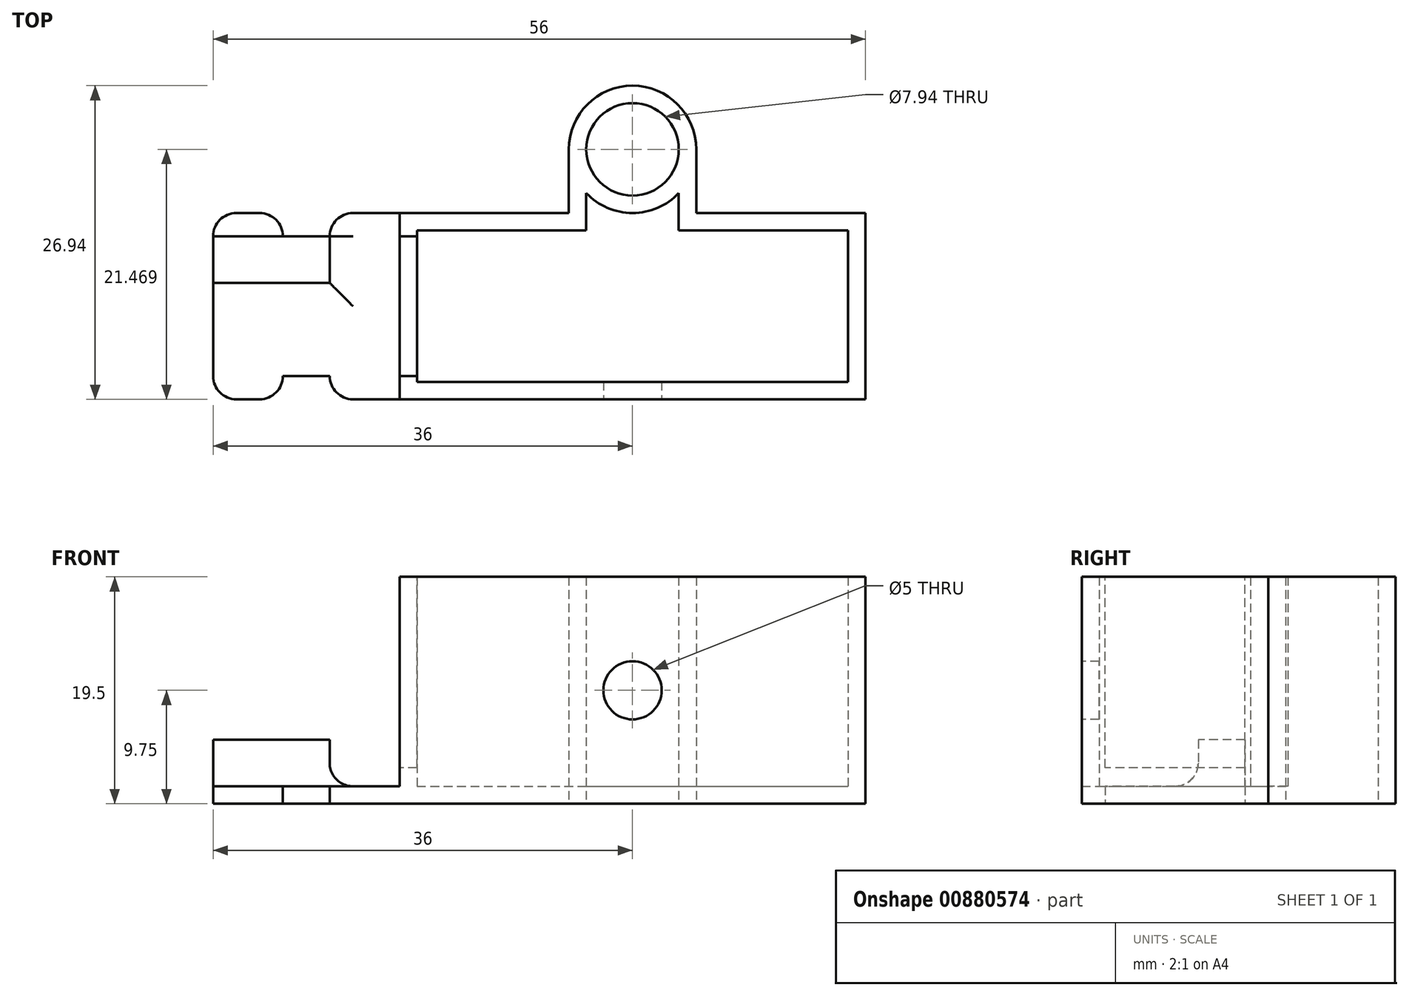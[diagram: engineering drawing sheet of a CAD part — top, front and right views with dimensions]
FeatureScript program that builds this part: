
annotation { "Feature Type Name" : "Feature", "Feature Type Description" : "" }
export const myFeature = defineFeature(function(context is Context, id is Id, definition is map)
    precondition{}
    {
        {
            var Q0;
            Q0=qCreatedBy(makeId("Top.planeOp"),FACE);
            var sketch = newSketch(context, id + "F0", { "sketchPlane" : qUnion([Q0])});
            skLineSegment(sketch, "E0.bottom", {"start": v(0, 0) * mm, "end": v(37, 0) * mm, "construction": true});
            skLineSegment(sketch, "E0.top", {"start": v(0, 13) * mm, "end": v(37, 13) * mm, "construction": true});
            skLineSegment(sketch, "E0.left", {"start": v(0, 0) * mm, "end": v(0, 13) * mm, "construction": true});
            skLineSegment(sketch, "E0.right", {"start": v(37, 0) * mm, "end": v(37, 13) * mm, "construction": true});
            skLineSegment(sketch, "E1.0", {"start": v(-1.5, -1.5) * mm, "end": v(-1.5, 14.5) * mm});
            skLineSegment(sketch, "E1.1", {"start": v(-1.5, -1.5) * mm, "end": v(38.5, -1.5) * mm});
            skLineSegment(sketch, "E1.2", {"start": v(38.5, -1.5) * mm, "end": v(38.5, 14.5) * mm});
            skLineSegment(sketch, "E1.3", {"start": v(-1.5, 14.5) * mm, "end": v(13.03, 14.5) * mm});
            skLineSegment(sketch, "E2", {"start": v(18.5, 14.5) * mm, "end": v(18.5, 25.44) * mm, "construction": true});
            skCircle(sketch, "E3", {"center": v(18.5, 19.97) * mm, "radius": 3.97 * mm});
            skArc(sketch, "E4.0", {"start": v(23.97, 19.97) * mm, "mid": v(18.5, 25.44) * mm, "end": v(13.03, 19.97) * mm});
            skLineSegment(sketch, "E5", {"start": v(23.97, 14.5) * mm, "end": v(23.97, 19.97) * mm});
            skLineSegment(sketch, "E6", {"start": v(13.03, 14.5) * mm, "end": v(13.03, 19.97) * mm});
            skLineSegment(sketch, "E7.trimOffspring", {"start": v(23.97, 14.5) * mm, "end": v(38.5, 14.5) * mm});
            skSolve(sketch);
        }
        {
            var Q0;
            Q0 = qSketchRegion(id + "F0", true);
            extrude(context, id + "F1", {"entities" : qUnion([Q0]), "depth" : 19.5 * mm, "offsetDistance" : 25 * mm});
        }
        {
            var Q0;
            Q0=makeQuery(id+"F1.opExtrude","CAP_FACE",FACE,{"disambiguationData":[OSD([sQuery(id+"F0.wireOp",EDGE,"E1.0"),sQuery(id+"F0.wireOp",EDGE,"E1.1"),sQuery(id+"F0.wireOp",EDGE,"E1.2"),sQuery(id+"F0.wireOp",EDGE,"E1.3"),sQuery(id+"F0.wireOp",EDGE,"E3"),sQuery(id+"F0.wireOp",EDGE,"E4.0"),sQuery(id+"F0.wireOp",EDGE,"E5"),sQuery(id+"F0.wireOp",EDGE,"E6"),sQuery(id+"F0.wireOp",EDGE,"E7.trimOffspring")])],"isStart":false});
            shell(context, id + "F2", {"entities" : qUnion([Q0]), "thickness" : 1.5 * mm});
        }
        {
            var Q0;
            Q0=makeQuery(id+"F1.opExtrude","SWEPT_FACE",FACE,{"disambiguationData":[OSD([sQuery(id+"F0.wireOp",EDGE,"E1.1")])]});
            var sketch = newSketch(context, id + "F3", { "sketchPlane" : qUnion([Q0])});
            skCircle(sketch, "E8", {"center": v(18.5, 9.75) * mm, "radius": 2.5 * mm});
            skLineSegment(sketch, "E9", {"start": v(-1.5, 9.75) * mm, "end": v(38.5, 9.75) * mm, "construction": true});
            skSolve(sketch);
        }
        {
            var Q0;
            Q0 = qSketchRegion(id + "F3", true);
            extrude(context, id + "F4", {"entities" : qUnion([Q0]), "operationType" : NewBodyOperationType.REMOVE, "oppositeDirection" : true, "depth" : 1.5 * mm, "offsetDistance" : 25 * mm});
        }
        {
            var Q0;
            Q0=makeQuery(id+"F1.opExtrude","CAP_FACE",FACE,{"disambiguationData":[OSD([sQuery(id+"F0.wireOp",EDGE,"E1.0"),sQuery(id+"F0.wireOp",EDGE,"E1.1"),sQuery(id+"F0.wireOp",EDGE,"E1.2"),sQuery(id+"F0.wireOp",EDGE,"E1.3"),sQuery(id+"F0.wireOp",EDGE,"E3"),sQuery(id+"F0.wireOp",EDGE,"E4.0"),sQuery(id+"F0.wireOp",EDGE,"E5"),sQuery(id+"F0.wireOp",EDGE,"E6"),sQuery(id+"F0.wireOp",EDGE,"E7.trimOffspring")])],"isStart":false});
            var sketch = newSketch(context, id + "F5", { "sketchPlane" : qUnion([Q0])});
            skLineSegment(sketch, "E10.bottom", {"start": v(-1.5, 12.5) * mm, "end": v(0, 12.5) * mm});
            skLineSegment(sketch, "E10.top", {"start": v(-1.5, 0.5) * mm, "end": v(0, 0.5) * mm});
            skLineSegment(sketch, "E10.left", {"start": v(-1.5, 12.5) * mm, "end": v(-1.5, 0.5) * mm});
            skLineSegment(sketch, "E10.right", {"start": v(0, 12.5) * mm, "end": v(0, 0.5) * mm});
            skLineSegment(sketch, "E11", {"start": v(-1.5, 6.5) * mm, "end": v(0, 6.5) * mm, "construction": true});
            skSolve(sketch);
        }
        {
            var Q0;
            Q0 = qSketchRegion(id + "F5", true);
            var Q1;
            Q1=makeQuery(id+"F2.opShell","OFFSET_FACE",FACE,{"disambiguationData":[OSD([sQuery(id+"F0.wireOp",EDGE,"E1.0"),sQuery(id+"F0.wireOp",EDGE,"E1.1"),sQuery(id+"F0.wireOp",EDGE,"E1.2"),sQuery(id+"F0.wireOp",EDGE,"E1.3"),sQuery(id+"F0.wireOp",EDGE,"E3"),sQuery(id+"F0.wireOp",EDGE,"E4.0"),sQuery(id+"F0.wireOp",EDGE,"E5"),sQuery(id+"F0.wireOp",EDGE,"E6"),sQuery(id+"F0.wireOp",EDGE,"E7.trimOffspring")])]});
            extrude(context, id + "F6", {"entities" : qUnion([Q0]), "operationType" : NewBodyOperationType.REMOVE, "endBound" : BoundingType.UP_TO_SURFACE, "oppositeDirection" : true, "depth" : 25 * mm, "endBoundEntityFace" : qUnion([Q1]), "hasOffset" : true, "offsetDistance" : 1.6 * mm});
        }
        {
            var Q0;
            Q0=makeQuery(id+"F1.opExtrude","CAP_FACE",FACE,{"disambiguationData":[OSD([sQuery(id+"F0.wireOp",EDGE,"E1.0"),sQuery(id+"F0.wireOp",EDGE,"E1.1"),sQuery(id+"F0.wireOp",EDGE,"E1.2"),sQuery(id+"F0.wireOp",EDGE,"E1.3"),sQuery(id+"F0.wireOp",EDGE,"E3"),sQuery(id+"F0.wireOp",EDGE,"E4.0"),sQuery(id+"F0.wireOp",EDGE,"E5"),sQuery(id+"F0.wireOp",EDGE,"E6"),sQuery(id+"F0.wireOp",EDGE,"E7.trimOffspring")])],"isStart":true});
            var sketch = newSketch(context, id + "F7", { "sketchPlane" : qUnion([Q0])});
            skLineSegment(sketch, "E12.bottom", {"start": v(-1.5, -14.5) * mm, "end": v(-17.5, -14.5) * mm, "construction": true});
            skLineSegment(sketch, "E12.top", {"start": v(-1.5, 1.5) * mm, "end": v(-17.5, 1.5) * mm, "construction": true});
            skLineSegment(sketch, "E12.left", {"start": v(-1.5, -14.5) * mm, "end": v(-1.5, 1.5) * mm});
            skLineSegment(sketch, "E12.right", {"start": v(-17.5, -14.5) * mm, "end": v(-17.5, 1.5) * mm});
            skLineSegment(sketch, "E13", {"start": v(-9.5, 1.5) * mm, "end": v(-9.5, -14.5) * mm, "construction": true});
            skLineSegment(sketch, "E14", {"start": v(-17.5, -6.5) * mm, "end": v(-1.5, -6.5) * mm, "construction": true});
            skLineSegment(sketch, "E15.top", {"start": v(-11.5, -0.5) * mm, "end": v(-7.5, -0.5) * mm});
            skLineSegment(sketch, "E15.left", {"start": v(-11.5, 1.5) * mm, "end": v(-11.5, -0.5) * mm});
            skLineSegment(sketch, "E15.right", {"start": v(-7.5, 1.5) * mm, "end": v(-7.5, -0.5) * mm});
            skLineSegment(sketch, "E16", {"start": v(-17.5, 1.5) * mm, "end": v(-11.5, 1.5) * mm});
            skLineSegment(sketch, "E17", {"start": v(-7.5, 1.5) * mm, "end": v(-1.5, 1.5) * mm});
            skLineSegment(sketch, "E18.MirrorCS", {"start": v(-7.5, -14.5) * mm, "end": v(-1.5, -14.5) * mm});
            skLineSegment(sketch, "E19.MirrorCS", {"start": v(-7.5, -14.5) * mm, "end": v(-7.5, -12.5) * mm});
            skLineSegment(sketch, "E20.MirrorCS", {"start": v(-11.5, -12.5) * mm, "end": v(-7.5, -12.5) * mm});
            skLineSegment(sketch, "E21.MirrorCS", {"start": v(-17.5, -14.5) * mm, "end": v(-11.5, -14.5) * mm});
            skLineSegment(sketch, "E22.MirrorCS", {"start": v(-11.5, -14.5) * mm, "end": v(-11.5, -12.5) * mm});
            skSolve(sketch);
        }
        {
            var Q0;
            Q0 = qSketchRegion(id + "F7", true);
            extrude(context, id + "F8", {"entities" : qUnion([Q0]), "operationType" : NewBodyOperationType.ADD, "oppositeDirection" : true, "depth" : 1.5 * mm, "offsetDistance" : 25 * mm});
        }
        {
            var Q0;
            Q0=makeQuery(id+"F8.opExtrude","SWEPT_EDGE",EDGE,{"disambiguationData":[OSD([sQuery(id+"F7.wireOp",EDGE,"E12.right"),sQuery(id+"F7.wireOp",EDGE,"E16")])]});
            var Q1;
            Q1=makeQuery(id+"F8.opExtrude","SWEPT_EDGE",EDGE,{"disambiguationData":[OSD([sQuery(id+"F7.wireOp",EDGE,"E15.left"),sQuery(id+"F7.wireOp",EDGE,"E16")])]});
            var Q2;
            Q2=makeQuery(id+"F8.opExtrude","SWEPT_EDGE",EDGE,{"disambiguationData":[OSD([sQuery(id+"F7.wireOp",EDGE,"E15.right"),sQuery(id+"F7.wireOp",EDGE,"E17")])]});
            var Q3;
            Q3=makeQuery(id+"F8.opExtrude","SWEPT_EDGE",EDGE,{"disambiguationData":[OSD([sQuery(id+"F7.wireOp",EDGE,"E12.right"),sQuery(id+"F7.wireOp",EDGE,"E21.MirrorCS")])]});
            var Q4;
            Q4=makeQuery(id+"F8.opExtrude","SWEPT_EDGE",EDGE,{"disambiguationData":[OSD([sQuery(id+"F7.wireOp",EDGE,"E21.MirrorCS"),sQuery(id+"F7.wireOp",EDGE,"E22.MirrorCS")])]});
            var Q5;
            Q5=makeQuery(id+"F8.opExtrude","SWEPT_EDGE",EDGE,{"disambiguationData":[OSD([sQuery(id+"F7.wireOp",EDGE,"E18.MirrorCS"),sQuery(id+"F7.wireOp",EDGE,"E19.MirrorCS")])]});
            var Q6;
            Q6=makeQuery(id+"F8.opExtrude","CAP_EDGE",EDGE,{"disambiguationData":[OSD([sQuery(id+"F7.wireOp",EDGE,"E12.left")])],"isStart":false});
            fillet(context, id + "F9", {"entities" : qUnion([Q0, Q1, Q2, Q3, Q4, Q5, Q6]), "radius" : 2 * mm, "tangentPropagation" : true, "allowEdgeOverflow" : false});
        }
        {
            var Q0;
            Q0=makeQuery(id+"F8.opExtrude","CAP_FACE",FACE,{"disambiguationData":[OSD([sQuery(id+"F7.wireOp",EDGE,"E12.left"),sQuery(id+"F7.wireOp",EDGE,"E12.right"),sQuery(id+"F7.wireOp",EDGE,"E15.top"),sQuery(id+"F7.wireOp",EDGE,"E15.left"),sQuery(id+"F7.wireOp",EDGE,"E15.right"),sQuery(id+"F7.wireOp",EDGE,"E16"),sQuery(id+"F7.wireOp",EDGE,"E17"),sQuery(id+"F7.wireOp",EDGE,"E18.MirrorCS"),sQuery(id+"F7.wireOp",EDGE,"E19.MirrorCS"),sQuery(id+"F7.wireOp",EDGE,"E20.MirrorCS"),sQuery(id+"F7.wireOp",EDGE,"E21.MirrorCS"),sQuery(id+"F7.wireOp",EDGE,"E22.MirrorCS")])],"isStart":false});
            var sketch = newSketch(context, id + "F10", { "sketchPlane" : qUnion([Q0])});
            skLineSegment(sketch, "E23.bottom", {"start": v(-17.5, 0.5) * mm, "end": v(-7.5, 0.5) * mm});
            skLineSegment(sketch, "E23.top", {"start": v(-17.5, 8.5) * mm, "end": v(-7.5, 8.5) * mm});
            skLineSegment(sketch, "E23.left", {"start": v(-17.5, 0.5) * mm, "end": v(-17.5, 8.5) * mm});
            skLineSegment(sketch, "E23.right", {"start": v(-7.5, 0.5) * mm, "end": v(-7.5, 8.5) * mm});
            skSolve(sketch);
        }
        {
            var Q0;
            {var subQ0=sQuery(id+"F7.wireOp",EDGE,"E21.MirrorCS");var subQ1=sQuery(id+"F7.wireOp",EDGE,"E17");var subQ2=sQuery(id+"F7.wireOp",EDGE,"E15.right");var subQ3=sQuery(id+"F7.wireOp",EDGE,"E20.MirrorCS");var subQ4=sQuery(id+"F7.wireOp",EDGE,"E18.MirrorCS");var subQ5=sQuery(id+"F7.wireOp",EDGE,"E12.left");var subQ6=sQuery(id+"F7.wireOp",EDGE,"E12.right");var subQ7=sQuery(id+"F7.wireOp",EDGE,"E15.top");var subQ8=sQuery(id+"F7.wireOp",EDGE,"E19.MirrorCS");var subQ9=sQuery(id+"F7.wireOp",EDGE,"E22.MirrorCS");Q0=makeQuery(id+"Fj0Jr3oSIS0SXok_1.boolean.opBoolean","SPLIT",FACE,{"disambiguationData":[TD([makeQuery(id+"F1.opExtrude","SWEPT_FACE",FACE,{"disambiguationData":[OSD([sQuery(id+"F0.wireOp",EDGE,"E1.1")])]})])],"derivedFrom":makeQuery(id+"F8.opExtrude","CAP_FACE",FACE,{"disambiguationData":[OSD([subQ5,subQ6,subQ7,sQuery(id+"F7.wireOp",EDGE,"E15.left"),subQ2,sQuery(id+"F7.wireOp",EDGE,"E16"),subQ1,subQ4,subQ8,subQ3,subQ0,subQ9])],"isStart":false})});}
            var sketch = newSketch(context, id + "F11", { "sketchPlane" : qUnion([Q0])});
            skLineSegment(sketch, "E24.bottom", {"start": v(-17.5, 8.5) * mm, "end": v(-7.5, 8.5) * mm});
            skLineSegment(sketch, "E24.top", {"start": v(-17.5, 12.5) * mm, "end": v(-7.5, 12.5) * mm});
            skLineSegment(sketch, "E24.left", {"start": v(-17.5, 8.5) * mm, "end": v(-17.5, 12.5) * mm});
            skLineSegment(sketch, "E24.right", {"start": v(-7.5, 8.5) * mm, "end": v(-7.5, 12.5) * mm});
            skSolve(sketch);
        }
        {
            var Q0;
            Q0 = qSketchRegion(id + "F11", true);
            extrude(context, id + "F12", {"entities" : qUnion([Q0]), "operationType" : NewBodyOperationType.ADD, "depth" : 4 * mm, "offsetDistance" : 25 * mm});
        }
        {
            var Q0;
            Q0=makeQuery(id+"F12.opExtrude","CAP_EDGE",EDGE,{"disambiguationData":[OSD([sQuery(id+"F11.wireOp",EDGE,"E24.bottom")])],"isStart":true});
            var Q1;
            Q1=makeQuery(id+"F12.opExtrude","CAP_EDGE",EDGE,{"disambiguationData":[OSD([sQuery(id+"F11.wireOp",EDGE,"E24.right")])],"isStart":true});
            fillet(context, id + "F13", {"entities" : qUnion([Q0, Q1]), "radius" : 2 * mm, "tangentPropagation" : true, "allowEdgeOverflow" : false});
        }
    });
